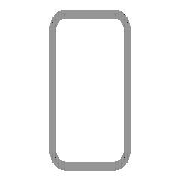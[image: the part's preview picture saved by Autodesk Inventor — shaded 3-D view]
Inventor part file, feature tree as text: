
AUTODESK INVENTOR PART (.ipt)
format: ipt  version: 2025.3 (Build 293356030, 356C)  size: 133,632 bytes
history: native  units: mm (DEFAULTED — no unit token found)
features: other x4, sketch x1, plane x1
ambient origin geometry x8: Origin, YZ Plane, XZ Plane, XY Plane, X Axis, Y Axis, Z Axis, Center Point
bodies: Solid1 (feature_tree), Body (feature_tree)
feature tree (6):
  parser-record x1  (decoder bookkeeping rows leaked as tree rows — omitted from the tree; the rows remain in map.json)
  other  "Driven Length"
  other  "Start Plane"
  other  "End Plane"
  sketch  "Sketch3"  dims[d3=750.0mm d4=0.0mm d7=4.0mm d9=20.0mm d11=40.0mm d12=2.0mm d13=40.0mm d14=790.0mm d15=10.0mm d16=20.0mm d17=90.0deg d18=750.0mm]
  plane  "Work Plane3"
